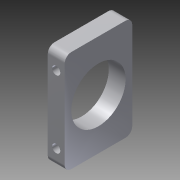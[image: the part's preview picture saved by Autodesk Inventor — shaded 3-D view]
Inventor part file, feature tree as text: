
AUTODESK INVENTOR PART (.ipt)
format: ipt  version: 2015 (Build 190159000, 159)  size: 126,976 bytes
history: native  units: mm
features: other x5, sketch x4
ambient origin geometry x8: Origin, YZ Plane, XZ Plane, XY Plane, X Axis, Y Axis, Z Axis, Center Point
bodies: Body1 (feature_tree)
feature tree (9):
  other  "support_caterpillar_spring_v1.3.ipt"
  other  "Sólido1::support_caterpillar_spring_v1.3.ipt"
  other  "OperaciónIdentificador1"
  sketch  "Boceto1"  dims[d0=10.0mm]
  other  "Axles"
  sketch  "Boceto4"
  sketch  "Boceto6"
  sketch  "Boceto10"
  other  "Sólido1"
